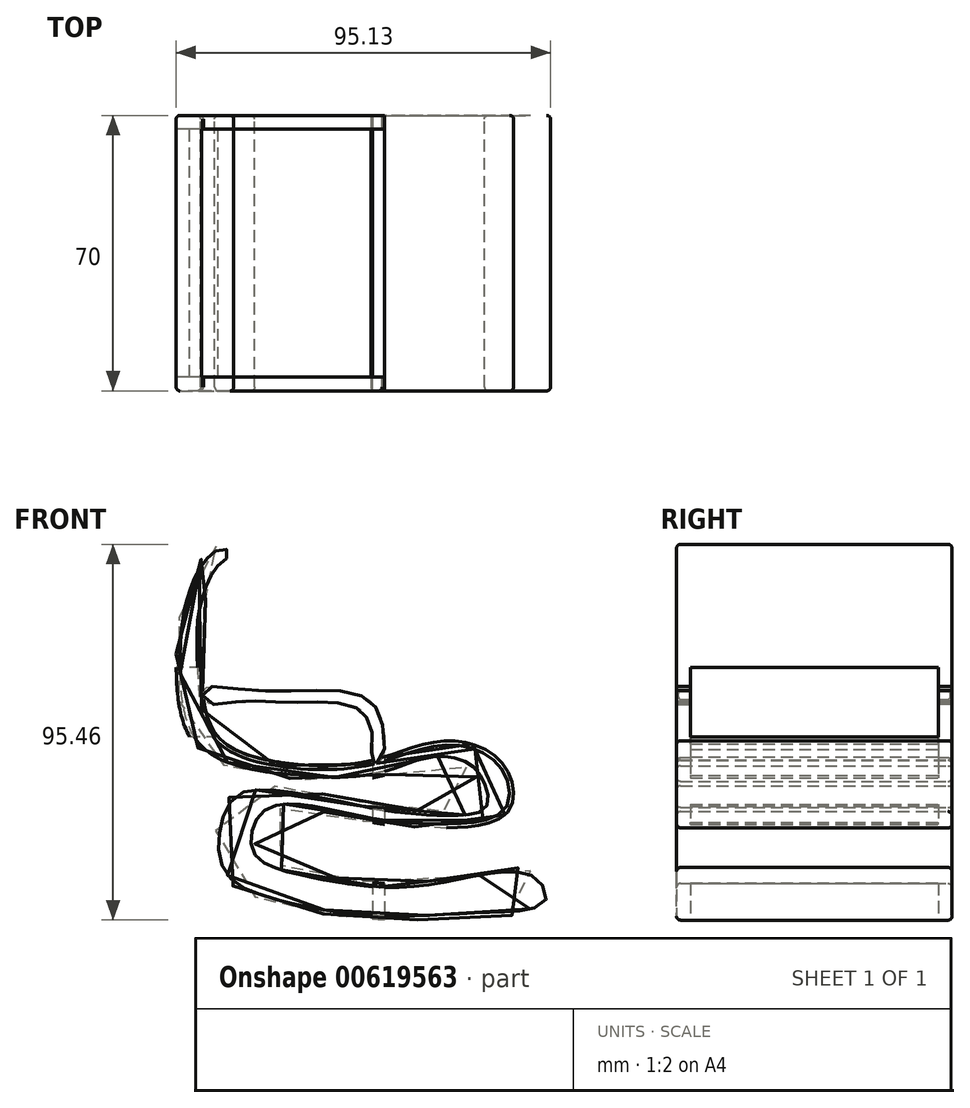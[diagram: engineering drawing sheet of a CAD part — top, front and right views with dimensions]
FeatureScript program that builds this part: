
annotation { "Feature Type Name" : "Feature", "Feature Type Description" : "" }
export const myFeature = defineFeature(function(context is Context, id is Id, definition is map)
    precondition{}
    {
        {
            var Q0;
            Q0=qCreatedBy(makeId("Front.planeOp"),FACE);
            var sketch = newSketch(context, id + "F0", { "sketchPlane" : qUnion([Q0])});
            skFitSpline(sketch, "E0", {"points": [v(-42.98, 46.27) * mm, v(-47.71, 34.95) * mm, v(-48.12, 22.4) * mm, v(-45.03, 4.9) * mm, v(-30.83, -2.72) * mm, v(-5.71, -2.93) * mm, v(13.43, 2.22) * mm, v(28.46, -3.54) * mm, v(29.7, -15.9) * mm, v(10.96, -19.8) * mm, v(-7.36, -17.96) * mm, v(-27.95, -14.87) * mm, v(-33.71, -19.2) * mm, v(-33.71, -25.98) * mm, v(-22.18, -30.92) * mm, v(7.67, -33.6) * mm, v(35.87, -30.92) * mm, v(40.2, -38.95) * mm, v(22.08, -42.45) * mm, v(4.17, -43.28) * mm, v(-13.13, -42.25) * mm, v(-32.27, -38.13) * mm, v(-42.36, -32.37) * mm, v(-44.62, -21.87) * mm, v(-40.1, -11.16) * mm, v(-29.8, -9.3) * mm, v(-11.68, -12.4) * mm, v(0, -14.66) * mm, v(16.93, -15.7) * mm, v(23.52, -13.84) * mm, v(22.9, -9.1) * mm, v(19.4, -4.37) * mm, v(10.34, -2.72) * mm, v(2.73, -5.2) * mm, v(-9.63, -7.87) * mm, v(-20.12, -7.66) * mm, v(-37, -5.6) * mm, v(-48.53, 0) * mm, v(-53.27, 9.01) * mm, v(-54.5, 22.19) * mm, v(-53.06, 37.22) * mm, v(-47.3, 49.36) * mm, v(-41.74, 52.04) * mm, v(-39.89, 49.36) * mm, v(-42.98, 46.27) * mm]});
            skSolve(sketch);
        }
        {
            var Q0;
            Q0 = qSketchRegion(id + "F0", true);
            extrude(context, id + "F1", {"entities" : qUnion([Q0]), "depth" : 70 * mm, "offsetDistance" : 25 * mm});
        }
        {
            var Q0;
            Q0=makeQuery(id+"F1.opExtrude","CAP_EDGE",EDGE,{"disambiguationData":[OSD([sQuery(id+"F0.wireOp",EDGE,"E0")])],"isStart":false});
            var Q1;
            Q1=makeQuery(id+"F1.opExtrude","CAP_EDGE",EDGE,{"disambiguationData":[OSD([sQuery(id+"F0.wireOp",EDGE,"E0")])],"isStart":true});
            fillet(context, id + "F2", {"entities" : qUnion([Q0, Q1]), "radius" : 1 * mm, "tangentPropagation" : true, "allowEdgeOverflow" : false});
        }
        {
            var Q0;
            Q0=qCreatedBy(makeId("Front.planeOp"),FACE);
            var sketch = newSketch(context, id + "F3", { "sketchPlane" : qUnion([Q0])});
            skFitSpline(sketch, "E1", {"points": [v(-47.45, 15.34) * mm, v(-37.78, 15.34) * mm, v(-24.4, 14.93) * mm, v(-12.87, 14.93) * mm, v(-5.25, 12.45) * mm, v(-2.16, 6.7) * mm, v(-2.37, -2.37) * mm, v(-4.63, -3.4) * mm, v(-4.63, 2.16) * mm, v(-5.87, 7.72) * mm, v(-8.13, 10.4) * mm, v(-15.13, 12.04) * mm, v(-22.75, 12.04) * mm, v(-31.6, 12.25) * mm, v(-38.8, 12.25) * mm, v(-46.83, 12.04) * mm, v(-47.45, 15.34) * mm]});
            skSolve(sketch);
        }
        {
            var Q0;
            Q0 = qSketchRegion(id + "F3", true);
            extrude(context, id + "F4", {"entities" : qUnion([Q0]), "operationType" : NewBodyOperationType.ADD, "depth" : 70 * mm, "offsetDistance" : 25 * mm});
        }
        {
            var Q0;
            Q0=qCreatedBy(makeId("Right.planeOp"),FACE);
            var sketch = newSketch(context, id + "F5", { "sketchPlane" : qUnion([Q0])});
            skLineSegment(sketch, "E2.bottom", {"start": v(-66.44, 20.96) * mm, "end": v(-3.48, 20.96) * mm});
            skLineSegment(sketch, "E2.top", {"start": v(-66.44, 3.29) * mm, "end": v(-3.48, 3.29) * mm});
            skLineSegment(sketch, "E2.left", {"start": v(-66.44, 20.96) * mm, "end": v(-66.44, 3.29) * mm});
            skLineSegment(sketch, "E2.right", {"start": v(-3.48, 20.96) * mm, "end": v(-3.48, 3.29) * mm});
            skSolve(sketch);
        }
        {
            var Q0;
            Q0 = qSketchRegion(id + "F5", true);
            extrude(context, id + "F6", {"entities" : qUnion([Q0]), "operationType" : NewBodyOperationType.REMOVE, "endBound" : BoundingType.THROUGH_ALL, "depth" : 70 * mm, "offsetDistance" : 25 * mm, "hasSecondDirection" : true, "secondDirectionOppositeDirection" : true, "secondDirectionDepth" : 70 * mm});
        }
        {
            var Q0;
            Q0=makeQuery(id+"F6.boolean.opBoolean","COPY",FACE,{"disambiguationData":[TD([makeQuery(id+"F4.opExtrude","SWEPT_FACE",FACE,{"disambiguationData":[OSD([sQuery(id+"F3.wireOp",EDGE,"E1")])]})])],"derivedFrom":makeQuery(id+"F6.opExtrude","SWEPT_FACE",FACE,{"disambiguationData":[OSD([sQuery(id+"F5.wireOp",EDGE,"E2.top")])]})});
            var sketch = newSketch(context, id + "F7", { "sketchPlane" : qUnion([Q0])});
            skLineSegment(sketch, "E3.bottom", {"start": v(-4.66, -3.48) * mm, "end": v(-1.6, -3.48) * mm});
            skLineSegment(sketch, "E3.top", {"start": v(-4.66, -66.44) * mm, "end": v(-1.6, -66.44) * mm});
            skLineSegment(sketch, "E3.left", {"start": v(-4.66, -3.48) * mm, "end": v(-4.66, -66.44) * mm});
            skLineSegment(sketch, "E3.right", {"start": v(-1.6, -3.48) * mm, "end": v(-1.6, -66.44) * mm});
            skSolve(sketch);
        }
        {
            var Q0;
            Q0 = qSketchRegion(id + "F7", true);
            extrude(context, id + "F8", {"entities" : qUnion([Q0]), "operationType" : NewBodyOperationType.REMOVE, "endBound" : BoundingType.THROUGH_ALL, "depth" : 25 * mm, "offsetDistance" : 25 * mm, "hasSecondDirection" : true, "secondDirectionOppositeDirection" : true, "secondDirectionDepth" : 80 * mm});
        }
    });
